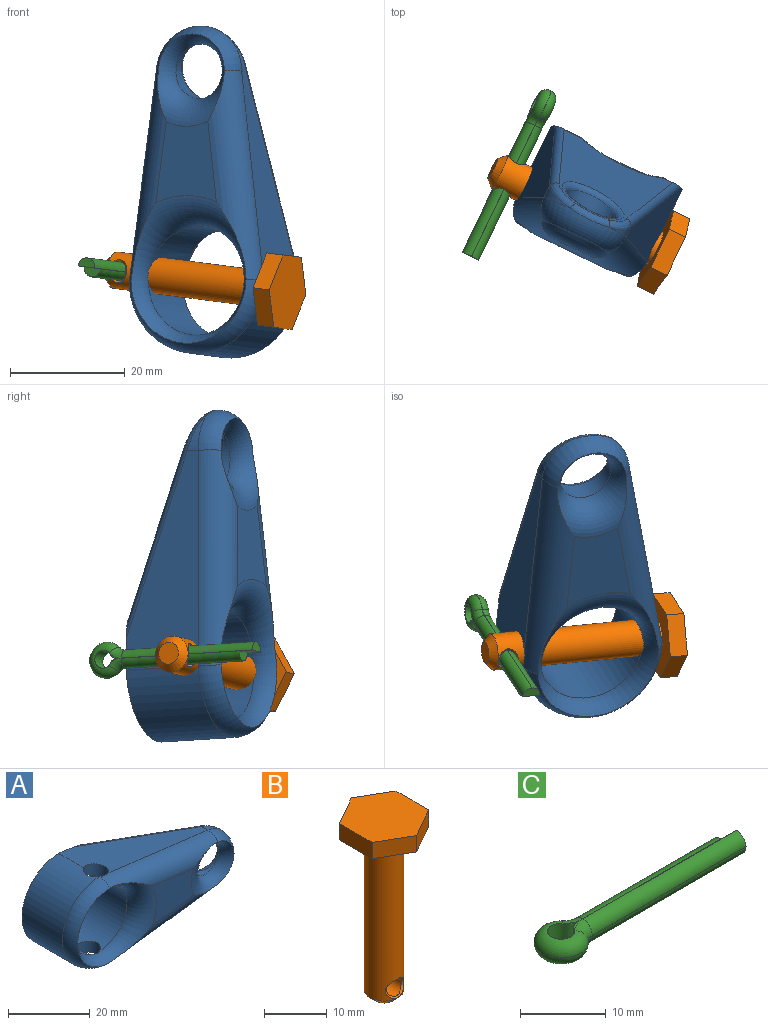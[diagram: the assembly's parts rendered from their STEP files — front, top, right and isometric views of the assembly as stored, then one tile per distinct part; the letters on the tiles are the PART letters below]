
ASSEMBLY  parts=3 mates=3
PART A: 30 faces, bbox 67.5x20.9x32.2 mm
  f0: plane 0.18x0.11mm, normal (0.13,0,0.99), area 0mm2, adj f5,f14,f28
  f1: cylinder r=12.7mm len=0.19mm, axis (0,1,0), area 0mm2, adj f6,f12,f29
  f2: cylinder r=7.94mm len=6.46mm, axis (0,1,0), area 6.9mm2, adj f6,f15,f26
  f3: plane 26.02x21.96mm, normal (0,1,0), area 160.7mm2, adj f4,f5,f6,f9,f20,f21,f23,f25
  f4: plane 37.53x13.97mm, normal (0.13,0,0.99), area 312.5mm2, adj f3,f5,f8,f14,f20,f28
  f5: cylinder r=12.7mm len=25.4mm, axis (0,1,0), area 527.9mm2, adj f0,f3,f4,f6,f12,f28,f29
  f6: plane 36.53x13.97mm, normal (0.13,0,-0.99), area 301.4mm2, adj f1,f2,f3,f5,f16,f26,f27,f29
  f7: cylinder r=4.76mm len=9.53mm, axis (0,1,0), area 64.1mm2, adj f17,f18
  f8: cylinder r=7.94mm len=6.4mm, axis (0,1,0), area 9.2mm2, adj f4,f15,f22
  f9: cylinder r=9.53mm len=19.05mm, axis (0,1,0), area 738mm2, adj f3,f13,f23,f28,f29
  f10: plane 14.16x11.69mm, normal (0,-1,0), area 125.2mm2, adj f13,f14,f16,f17
  f11: plane 37.29x20.97mm, normal (0.34,0.94,-0.04), area 444.7mm2, adj f18,f19,f20,f21,f22,f23,f24,f25
  f12: torus R=7.62mm, axis (0,-1,0), area 156.6mm2, adj f1,f5,f13,f14,f16,f29
  f13: torus R=14.61mm, axis (0,-1,0), area 330.6mm2, adj f9,f10,f12,f14,f16,f28,f29
  f14: cylinder r=5.08mm len=38.17mm, axis (0.99,0,-0.13), area 239.7mm2, adj f0,f4,f10,f12,f13,f15,f17,f28
  f15: torus R=2.86mm, axis (0,-1,0), area 90.3mm2, adj f2,f8,f14,f16,f17,f24
  f16: cylinder r=5.08mm len=37.28mm, axis (-0.99,0,-0.13), area 239.8mm2, adj f6,f10,f12,f13,f15,f17
  f17: torus R=9.84mm, axis (0,-1,0), area 190.9mm2, adj f7,f10,f14,f15,f16,f19
  f18: bspline ~12.06x12.03mm, area 62.3mm2, adj f7,f11,f19
  f19: bspline ~5.12x2.45mm, area 5.7mm2, adj f11,f17,f18
  f20: cylinder r=1.27mm len=32.54mm, axis (-0.93,0.34,0.12), area 64.5mm2, adj f3,f4,f11,f21,f22
  f21: cylinder r=1.27mm len=3.94mm, axis (0.13,0,0.99), area 1.6mm2, adj f3,f11,f20,f23
  f22: bspline ~6.4x5.55mm, area 14.8mm2, adj f8,f11,f20,f24
  f23: bspline ~20.11x9.12mm, area 47.5mm2, adj f3,f9,f11,f21,f25
  f24: bspline ~8.94x2.97mm, area 12mm2, adj f11,f15,f22,f26
  f25: cylinder r=1.27mm len=2.56mm, axis (0.13,0,0.99), area 1mm2, adj f3,f11,f23,f27
  f26: bspline ~6.55x4.01mm, area 12.9mm2, adj f2,f6,f11,f24,f27
  f27: cylinder r=1.27mm len=34.41mm, axis (0.94,-0.33,0.12), area 64.7mm2, adj f3,f6,f11,f25,f26
  f28: cylinder r=3.08mm len=6.58mm, axis (0.13,0,0.99), area 63.4mm2, adj f0,f4,f5,f9,f13,f14
  f29: cylinder r=3.08mm len=6.59mm, axis (0.13,0,0.99), area 62.3mm2, adj f1,f5,f6,f9,f12,f13
PART B: 14 faces, bbox 12.7x14.7x34.9 mm
  f0: cylinder r=3.17mm len=30.48mm, axis (0,0,-1), area 583.5mm2, adj f1,f11,f12,f13
  f1: plane 14.66x12.7mm, normal (0,0,-1), area 108mm2, adj f0,f2,f3,f4,f5,f6,f7
  f2: plane 6.35x3.67mm, normal (0.5,0.87,0), area 23.3mm2, adj f1,f3,f7,f8
  f3: plane 6.35x3.67mm, normal (-0.5,0.87,0), area 23.3mm2, adj f1,f2,f4,f8
  f4: plane 7.33x3.18mm, normal (-1,0,0), area 23.3mm2, adj f1,f3,f5,f8
  f5: plane 6.35x3.67mm, normal (-0.5,-0.87,0), area 23.3mm2, adj f1,f4,f6,f8
  f6: plane 6.35x3.67mm, normal (0.5,-0.87,0), area 23.3mm2, adj f1,f5,f7,f8
  f7: plane 7.33x3.18mm, normal (1,0,0), area 23.3mm2, adj f1,f2,f6,f8
  f8: plane 14.66x12.7mm, normal (0,0,1), area 139.7mm2, adj f2,f3,f4,f5,f6,f7
  f9: plane 3.81x3.81mm, normal (0,0,-1), area 11.4mm2, adj f13
  f10: cylinder r=1.59mm len=5.84mm, axis (0,-1,0), area 58.2mm2, adj f11,f12
  f11: bspline ~4x3.68mm, area 4.7mm2, adj f0,f10
  f12: bspline ~4.02x3.7mm, area 4.7mm2, adj f0,f10
  f13: cone r=3.17mm half-angle=45deg, axis (0,0,1), area 28.7mm2, adj f0,f9
PART C: 23 faces, bbox 32.4x6.9x3.2 mm
  f0: cylinder r=1.59mm len=3.18mm, axis (0,0,-1), area 26.4mm2, adj f1,f10,f11,f12
  f1: cylinder r=1.59mm len=3.18mm, axis (0,0,-1), area 5.3mm2, adj f0,f10,f11,f12
  f2: plane 3.18x2.55mm, normal (0,1,0), area 8.1mm2, adj f3,f9,f11,f12
  f3: plane 3.18x1.59mm, normal (1,0,0), area 4mm2, adj f2,f4,f11,f12,f13,f22
  f4: plane 22.85x0.03mm, normal (0,1,0), area 0.6mm2, adj f3,f5,f13,f22
  f5: cylinder r=1.59mm len=1.18mm, axis (0,0,-1), area 0mm2, adj f4,f6,f14,f21
  f6: cylinder r=3.17mm len=6.35mm, axis (0,0,-1), area 0.4mm2, adj f5,f7,f15,f20
  f7: cylinder r=1.59mm len=1.18mm, axis (0,0,-1), area 0mm2, adj f6,f8,f16,f19
  f8: plane 25.4x0.03mm, normal (0,-1,0), area 0.6mm2, adj f7,f9,f17,f18
  f9: plane 3.18x1.59mm, normal (1,0,0), area 4mm2, adj f2,f8,f11,f12,f17,f18
  f10: cylinder r=1.59mm len=3.18mm, axis (0,0,-1), area 5.3mm2, adj f0,f1,f11,f12
  f11: plane 30.55x3.2mm, normal (0,0,1), area 1.3mm2, adj f0,f1,f2,f3,f9,f10,f13,f14
  f12: plane 30.55x3.2mm, normal (0,0,-1), area 1.3mm2, adj f0,f1,f2,f3,f9,f10,f18,f19
  f13: cylinder r=1.57mm len=22.85mm, axis (1,0,0), area 56.5mm2, adj f3,f4,f11,f14
  f14: torus R=3.16mm, axis (0,0,1), area 4.5mm2, adj f5,f11,f13,f15
  f15: torus R=1.6mm, axis (0,0,1), area 31.1mm2, adj f6,f11,f14,f16
  f16: torus R=3.16mm, axis (0,0,1), area 4.5mm2, adj f7,f11,f15,f17
  f17: cylinder r=1.57mm len=25.4mm, axis (-1,0,0), area 62.8mm2, adj f8,f9,f11,f16
  f18: cylinder r=1.57mm len=25.4mm, axis (1,0,0), area 62.8mm2, adj f8,f9,f12,f19
  f19: torus R=3.16mm, axis (0,0,1), area 4.5mm2, adj f7,f12,f18,f20
  f20: torus R=1.6mm, axis (0,0,1), area 31.1mm2, adj f6,f12,f19,f21
  f21: torus R=3.16mm, axis (0,0,1), area 4.5mm2, adj f5,f12,f20,f22
  f22: cylinder r=1.57mm len=22.85mm, axis (-1,0,0), area 56.5mm2, adj f3,f4,f12,f21
PLACE A rot(axis=(-0.25,-0.95,-0.19),92.9deg) t=(72.55,-78.11,-79.66)mm
PLACE B rot(axis=(0.74,-0.15,0.65),160.6deg) t=(56.05,-90.36,-53.21)mm
PLACE C rot(axis=(-0.44,0.66,-0.61),140.8deg) t=(59.52,-67.82,-70.61)mm
MATE cylindrical B.f0 <-> A.f28  axis (-0.89,0.44,0.11) through (50.96,-80.01,-76.88)mm
MATE cylindrical C.f17 <-> B.f10  axis (-0.43,-0.9,0.06) through (47.05,-95.32,-76.48)mm
MATE cylindrical C.f17 <-> B.f10  axis (-0.43,-0.9,0.06) through (47.05,-95.32,-76.48)mm
